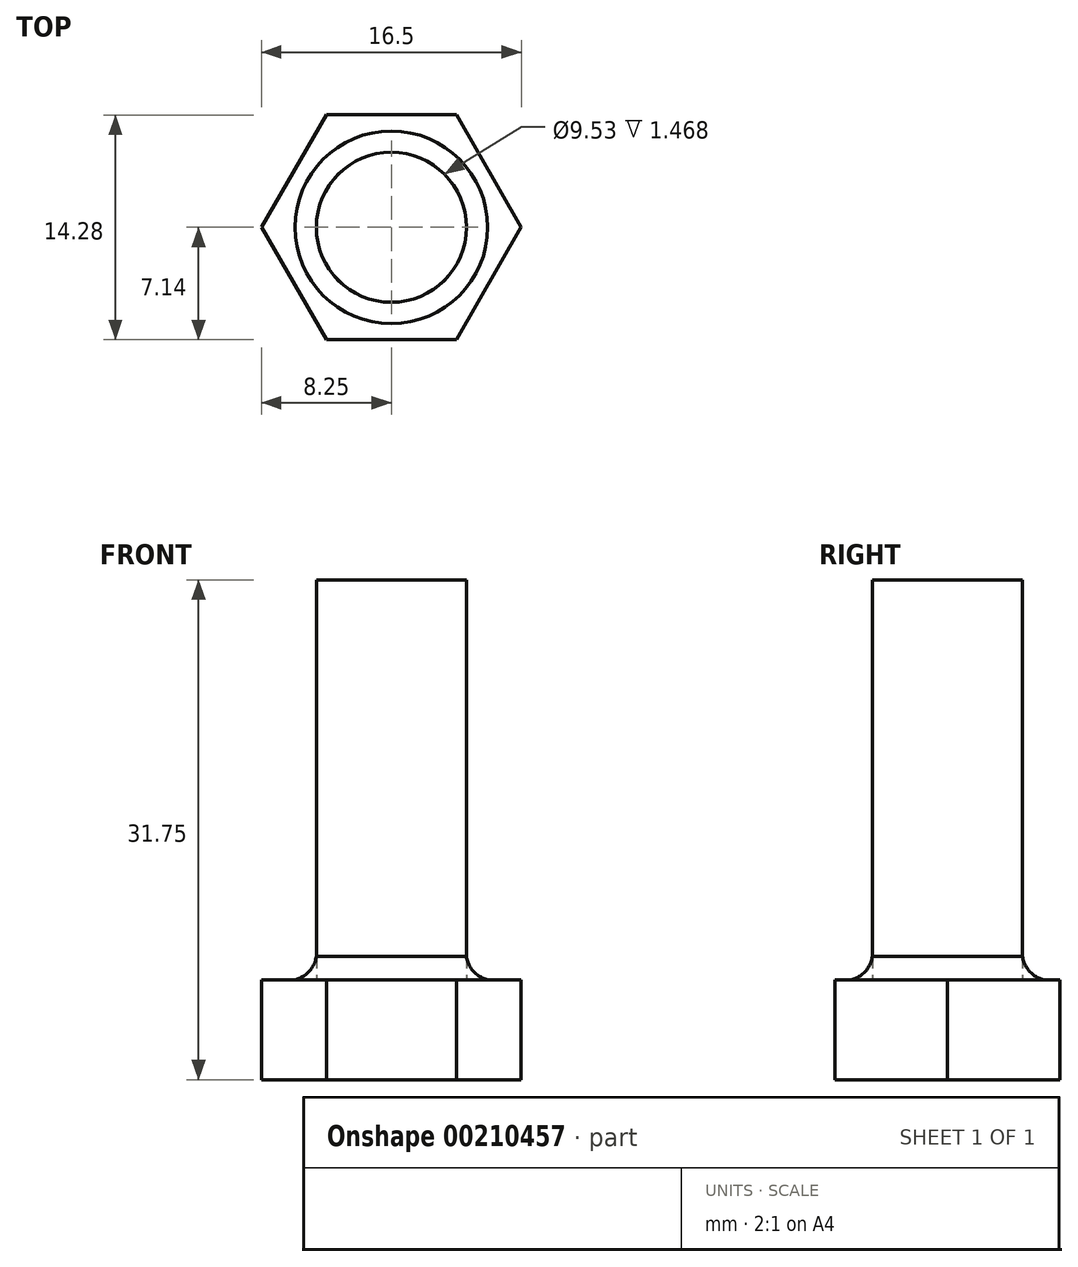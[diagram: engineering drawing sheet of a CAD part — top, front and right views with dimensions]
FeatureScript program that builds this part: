
annotation { "Feature Type Name" : "Feature", "Feature Type Description" : "" }
export const myFeature = defineFeature(function(context is Context, id is Id, definition is map)
    precondition{}
    {
        {
            var Q0;
            Q0=qCreatedBy(makeId("Top.planeOp"),FACE);
            var sketch = newSketch(context, id + "F0", { "sketchPlane" : qUnion([Q0])});
            skCircle(sketch, "E0.cCircle", {"center": v(0, 0) * mm, "radius": 7.14 * mm, "construction": true});
            skLineSegment(sketch, "E0.0", {"start": v(-4.12, 7.14) * mm, "end": v(4.12, 7.14) * mm});
            skLineSegment(sketch, "E0.1", {"start": v(4.12, 7.14) * mm, "end": v(8.25, 0) * mm});
            skLineSegment(sketch, "E0.2", {"start": v(8.25, 0) * mm, "end": v(4.12, -7.14) * mm});
            skLineSegment(sketch, "E0.3", {"start": v(4.12, -7.14) * mm, "end": v(-4.12, -7.14) * mm});
            skLineSegment(sketch, "E0.4", {"start": v(-4.12, -7.14) * mm, "end": v(-8.25, 0) * mm});
            skLineSegment(sketch, "E0.5", {"start": v(-8.25, 0) * mm, "end": v(-4.12, 7.14) * mm});
            skPoint(sketch, "E0.0.midPoint", {"position": v(0, 7.14) * mm});
            skSolve(sketch);
        }
        {
            var Q0;
            Q0=makeQuery(id+"F0.imprint","IMPRINT",FACE,{"disambiguationData":[TD([[makeQuery(id+"F0.imprint","IMPRINT",EDGE,{"derivedFrom":sQuery(id+"F0.wireOp",EDGE,"E0.0")}),-1.0]])]});
            extrude(context, id + "F1", {"entities" : qUnion([Q0]), "oppositeDirection" : true, "depth" : 6.35 * mm});
        }
        {
            var Q0;
            Q0=makeQuery(id+"F1.opExtrude","CAP_FACE",FACE,{"disambiguationData":[OSD([sQuery(id+"F0.wireOp",EDGE,"E0.0"),sQuery(id+"F0.wireOp",EDGE,"E0.1"),sQuery(id+"F0.wireOp",EDGE,"E0.2"),sQuery(id+"F0.wireOp",EDGE,"E0.3"),sQuery(id+"F0.wireOp",EDGE,"E0.4"),sQuery(id+"F0.wireOp",EDGE,"E0.5")])],"isStart":true});
            var sketch = newSketch(context, id + "F2", { "sketchPlane" : qUnion([Q0])});
            skCircle(sketch, "E1", {"center": v(0, 0) * mm, "radius": 4.76 * mm});
            skSolve(sketch);
        }
        {
            var Q0;
            Q0=makeQuery(id+"F2.imprint","IMPRINT",FACE,{"disambiguationData":[TD([[makeQuery(id+"F2.imprint","IMPRINT",EDGE,{"derivedFrom":sQuery(id+"F2.wireOp",EDGE,"E1")}),1.0]])]});
            var Q1;
            Q1=sQuery(id+"F2.wireOp",EDGE,"E1");
            extrude(context, id + "F3", {"entities" : qUnion([Q0]), "surfaceEntities" : qUnion([Q1]), "depth" : 25.4 * mm});
        }
        {
            var Q0;
            Q0=qCreatedBy(makeId("Front.planeOp"),FACE);
            var sketch = newSketch(context, id + "F4", { "sketchPlane" : qUnion([Q0])});
            skArc(sketch, "E2", {"start": v(4.77, 1.47) * mm, "mid": v(5.22, 0.53) * mm, "end": v(6.12, 0) * mm});
            skLineSegment(sketch, "E3", {"start": v(4.77, 1.47) * mm, "end": v(4.77, 0) * mm});
            skLineSegment(sketch, "E4", {"start": v(4.77, 0) * mm, "end": v(6.12, 0) * mm});
            skLineSegment(sketch, "E5", {"start": v(0, 0) * mm, "end": v(0, 3.87) * mm});
            skSolve(sketch);
        }
        {
            var Q0;
            Q0=makeQuery(id+"F4.imprint","IMPRINT",FACE,{"disambiguationData":[TD([[makeQuery(id+"F4.imprint","IMPRINT",EDGE,{"derivedFrom":sQuery(id+"F4.wireOp",EDGE,"E2")}),-1.0]])]});
            var Q1;
            Q1=sQuery(id+"F4.wireOp",EDGE,"E5");
            revolve(context, id + "F5", {"operationType" : NewBodyOperationType.ADD, "entities" : qUnion([Q0]), "axis" : qUnion([Q1]), "revolveType" : RevolveType.FULL});
        }
    });
